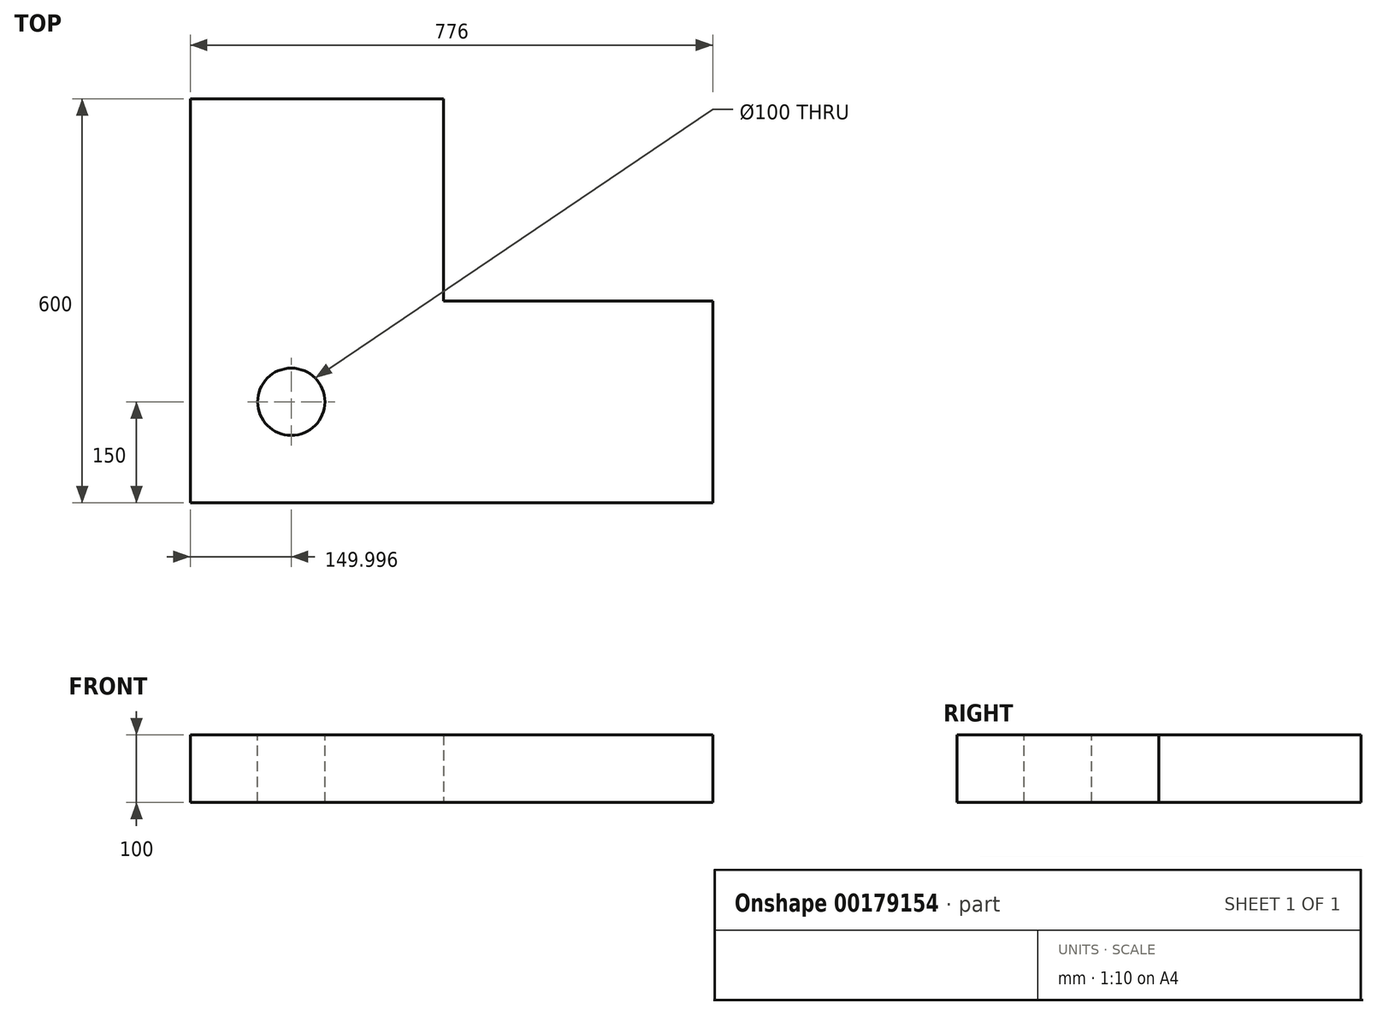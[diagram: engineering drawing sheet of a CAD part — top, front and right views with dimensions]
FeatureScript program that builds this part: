
annotation { "Feature Type Name" : "Feature", "Feature Type Description" : "" }
export const myFeature = defineFeature(function(context is Context, id is Id, definition is map)
    precondition{}
    {
        {
            var Q0;
            Q0=qCreatedBy(makeId("Top.planeOp"),FACE);
            var sketch = newSketch(context, id + "F0", { "sketchPlane" : qUnion([Q0])});
            skLineSegment(sketch, "E0", {"start": v(169, 0) * mm, "end": v(-207, 0) * mm});
            skLineSegment(sketch, "E1", {"start": v(-207, 0) * mm, "end": v(-207, -600) * mm});
            skLineSegment(sketch, "E2", {"start": v(-207, -600) * mm, "end": v(569, -600) * mm});
            skLineSegment(sketch, "E3", {"start": v(569, -600) * mm, "end": v(569, -300) * mm});
            skLineSegment(sketch, "E4", {"start": v(569, -300) * mm, "end": v(169, -300) * mm});
            skLineSegment(sketch, "E5", {"start": v(169, -300) * mm, "end": v(169, 0) * mm});
            skSolve(sketch);
        }
        {
            var Q0;
            Q0=makeQuery(id+"F0.imprint","IMPRINT",FACE,{"disambiguationData":[TD([[makeQuery(id+"F0.imprint","IMPRINT",EDGE,{"derivedFrom":sQuery(id+"F0.wireOp",EDGE,"E0")}),1.0]])]});
            extrude(context, id + "F1", {"entities" : qUnion([Q0]), "depth" : 100 * mm});
        }
        {
            var Q0;
            Q0=makeQuery(id+"F1.opExtrude","CAP_FACE",FACE,{"disambiguationData":[OSD([sQuery(id+"F0.wireOp",EDGE,"E0"),sQuery(id+"F0.wireOp",EDGE,"E1"),sQuery(id+"F0.wireOp",EDGE,"E2"),sQuery(id+"F0.wireOp",EDGE,"E3"),sQuery(id+"F0.wireOp",EDGE,"E4"),sQuery(id+"F0.wireOp",EDGE,"E5")])],"isStart":false});
            var sketch = newSketch(context, id + "F2", { "sketchPlane" : qUnion([Q0])});
            skLineSegment(sketch, "E6", {"start": v(569, -600) * mm, "end": v(569, -450) * mm, "construction": true});
            skLineSegment(sketch, "E7", {"start": v(-207, -600) * mm, "end": v(-57, -600) * mm, "construction": true});
            skLineSegment(sketch, "E8", {"start": v(-57, -600) * mm, "end": v(-57, -450) * mm});
            skCircle(sketch, "E9", {"center": v(-57, -450) * mm, "radius": 50 * mm});
            skSolve(sketch);
        }
        {
            var Q0;
            Q0=makeQuery(id+"F2.imprint","IMPRINT",FACE,{"disambiguationData":[TD([[makeQuery(id+"F2.imprint","IMPRINT",EDGE,{"derivedFrom":sQuery(id+"F2.wireOp",EDGE,"E9")}),1.0]])]});
            extrude(context, id + "F3", {"entities" : qUnion([Q0]), "operationType" : NewBodyOperationType.REMOVE, "oppositeDirection" : true, "depth" : 220.98 * mm});
        }
    });
